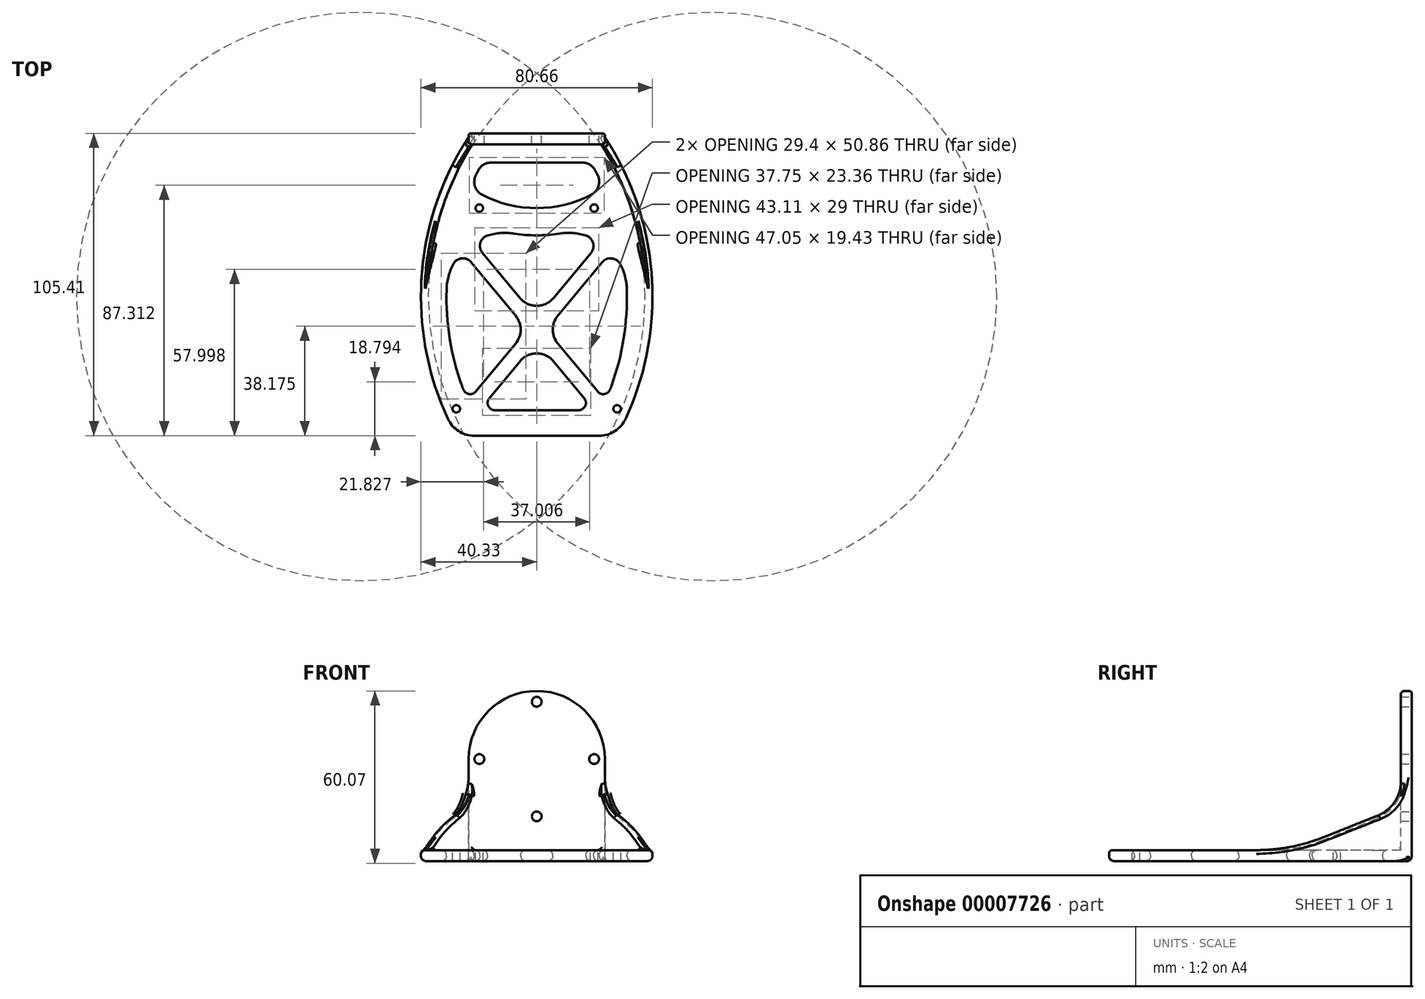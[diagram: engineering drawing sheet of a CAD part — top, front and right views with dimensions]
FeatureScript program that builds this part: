
annotation { "Feature Type Name" : "Feature", "Feature Type Description" : "" }
export const myFeature = defineFeature(function(context is Context, id is Id, definition is map)
    precondition{}
    {
        {
            var Q0;
            Q0=qCreatedBy(makeId("Front.planeOp"),FACE);
            var sketch = newSketch(context, id + "F0", { "sketchPlane" : qUnion([Q0])});
            skCircle(sketch, "E0", {"center": v(0, 19.99) * mm, "radius": 1.7 * mm});
            skCircle(sketch, "E1.1.0", {"center": v(-19.99, 0) * mm, "radius": 1.7 * mm});
            skCircle(sketch, "E1.2.0", {"center": v(0, -19.99) * mm, "radius": 1.7 * mm});
            skCircle(sketch, "E1.3.0", {"center": v(19.99, 0) * mm, "radius": 1.7 * mm});
            skPoint(sketch, "E1.center", {"position": v(0, 0) * mm});
            skArc(sketch, "E2", {"start": v(23.75, 0) * mm, "mid": v(0, 23.75) * mm, "end": v(-23.75, 0) * mm});
            skLineSegment(sketch, "E3.top", {"start": v(-23.75, -31.75) * mm, "end": v(23.75, -31.75) * mm});
            skLineSegment(sketch, "E3.left", {"start": v(-23.75, 0) * mm, "end": v(-23.75, -31.75) * mm});
            skLineSegment(sketch, "E3.right", {"start": v(23.75, 0) * mm, "end": v(23.75, -31.75) * mm});
            skSolve(sketch);
        }
        {
            var Q0;
            Q0 = qSketchRegion(id + "F0", true);
            extrude(context, id + "F1", {"entities" : qUnion([Q0]), "depth" : 2.54 * mm});
        }
        {
            var Q0;
            Q0=makeQuery(id+"F1.opExtrude","SWEPT_FACE",FACE,{"disambiguationData":[OSD([sQuery(id+"F0.wireOp",EDGE,"E3.top")])]});
            var sketch = newSketch(context, id + "F2", { "sketchPlane" : qUnion([Q0])});
            skCircle(sketch, "E4", {"center": v(-20, 24.77) * mm, "radius": 1.3 * mm});
            skCircle(sketch, "E5", {"center": v(-28, 94.77) * mm, "radius": 1.3 * mm});
            skLineSegment(sketch, "E6", {"start": v(-20, 24.77) * mm, "end": v(-20, 0) * mm, "construction": true});
            skLineSegment(sketch, "E7", {"start": v(-28, 94.77) * mm, "end": v(-28, 0) * mm, "construction": true});
            skCircle(sketch, "E8.0.MirrorC", {"center": v(20, 24.77) * mm, "radius": 1.3 * mm});
            skCircle(sketch, "E8.1.MirrorC", {"center": v(28, 94.77) * mm, "radius": 1.3 * mm});
            skArc(sketch, "E9", {"start": v(-30.96, 98.24) * mm, "mid": v(-40.06, 48.19) * mm, "end": v(-23.75, 0) * mm});
            skArc(sketch, "E10.0.MirrorCS", {"start": v(30.96, 98.24) * mm, "mid": v(40.06, 48.19) * mm, "end": v(23.75, 0) * mm});
            skLineSegment(sketch, "E11", {"start": v(-21.74, 104.14) * mm, "end": v(21.74, 104.14) * mm});
            skPoint(sketch, "E12.visualSharp", {"position": v(-28, 104.14) * mm});
            skArc(sketch, "E12.filletArc", {"start": v(-21.74, 104.14) * mm, "mid": v(-27.22, 102.54) * mm, "end": v(-30.96, 98.24) * mm});
            skPoint(sketch, "E13.visualSharp", {"position": v(28, 104.14) * mm});
            skArc(sketch, "E13.filletArc", {"start": v(30.96, 98.24) * mm, "mid": v(27.22, 102.54) * mm, "end": v(21.74, 104.14) * mm});
            skLineSegment(sketch, "E14", {"start": v(-23.75, 0) * mm, "end": v(23.75, 0) * mm});
            skArc(sketch, "E15.0", {"start": v(-26.04, 86.82) * mm, "mid": v(-30.28, 70.26) * mm, "end": v(-31.41, 53.2) * mm});
            skLineSegment(sketch, "E15.1", {"start": v(-14.08, 95.25) * mm, "end": v(14.08, 95.25) * mm});
            skArc(sketch, "E15.2", {"start": v(26.04, 86.82) * mm, "mid": v(30.28, 70.26) * mm, "end": v(31.41, 53.2) * mm});
            skLineSegment(sketch, "E15.3", {"start": v(-15.83, 8.89) * mm, "end": v(15.83, 8.89) * mm});
            skArc(sketch, "E16", {"start": v(7.93, 33.67) * mm, "mid": v(0, 34.3) * mm, "end": v(-7.93, 33.67) * mm});
            skArc(sketch, "E17", {"start": v(19.03, 20.12) * mm, "mid": v(0, 24.77) * mm, "end": v(-19.03, 20.12) * mm});
            skArc(sketch, "E18.trimOffspring", {"start": v(21.2, 13.29) * mm, "mid": v(20.76, 12.42) * mm, "end": v(20.3, 11.55) * mm});
            skArc(sketch, "E19.trimOffspring", {"start": v(-21.2, 13.29) * mm, "mid": v(-20.76, 12.42) * mm, "end": v(-20.3, 11.55) * mm});
            skPoint(sketch, "E20.visualSharp", {"position": v(-26.8, 26.65) * mm});
            skArc(sketch, "E20.filletArc", {"start": v(-31.41, 53.2) * mm, "mid": v(-30.77, 48.64) * mm, "end": v(-29.1, 44.33) * mm});
            skPoint(sketch, "E21.visualSharp", {"position": v(26.8, 26.65) * mm});
            skArc(sketch, "E21.filletArc", {"start": v(7.93, 33.67) * mm, "mid": v(12.55, 33.47) * mm, "end": v(17.1, 34.32) * mm});
            skPoint(sketch, "E22.visualSharp", {"position": v(18.8, 8.89) * mm});
            skArc(sketch, "E22.filletArc", {"start": v(15.83, 8.89) * mm, "mid": v(18.43, 9.6) * mm, "end": v(20.3, 11.55) * mm});
            skPoint(sketch, "E23.visualSharp", {"position": v(-18.8, 8.89) * mm});
            skArc(sketch, "E23.filletArc", {"start": v(-20.3, 11.55) * mm, "mid": v(-18.43, 9.6) * mm, "end": v(-15.83, 8.89) * mm});
            skPoint(sketch, "E24.visualSharp", {"position": v(-23.27, 17.58) * mm});
            skArc(sketch, "E24.filletArc", {"start": v(-19.03, 20.12) * mm, "mid": v(-21.53, 17.15) * mm, "end": v(-21.2, 13.29) * mm});
            skPoint(sketch, "E25.visualSharp", {"position": v(23.27, 17.58) * mm});
            skArc(sketch, "E25.filletArc", {"start": v(21.2, 13.29) * mm, "mid": v(21.53, 17.15) * mm, "end": v(19.03, 20.12) * mm});
            skPoint(sketch, "E26.visualSharp", {"position": v(-22.55, 95.25) * mm});
            skArc(sketch, "E26.filletArc", {"start": v(-14.08, 95.25) * mm, "mid": v(-14.4, 95.25) * mm, "end": v(-14.73, 95.23) * mm});
            skPoint(sketch, "E27.visualSharp", {"position": v(22.55, 95.25) * mm});
            skArc(sketch, "E27.filletArc", {"start": v(26.04, 86.82) * mm, "mid": v(25.76, 87.54) * mm, "end": v(25.43, 88.24) * mm});
            skLineSegment(sketch, "E28", {"start": v(-21.4, 92.93) * mm, "end": v(24.1, 38.12) * mm, "construction": true});
            skLineSegment(sketch, "E29", {"start": v(-24.1, 38.12) * mm, "end": v(21.4, 92.93) * mm, "construction": true});
            skLineSegment(sketch, "E30.0", {"start": v(-21.2, 88.73) * mm, "end": v(-7.34, 72.02) * mm});
            skLineSegment(sketch, "E31.0", {"start": v(-16.55, 91.07) * mm, "end": v(-5.86, 78.2) * mm});
            skLineSegment(sketch, "E32.0", {"start": v(-18.9, 40.4) * mm, "end": v(-5.86, 56.1) * mm});
            skLineSegment(sketch, "E33.0", {"start": v(-22.8, 43.66) * mm, "end": v(-7.34, 62.29) * mm});
            skArc(sketch, "E34.trimOffspring", {"start": v(14.73, 95.23) * mm, "mid": v(14.4, 95.25) * mm, "end": v(14.08, 95.25) * mm});
            skArc(sketch, "E35.trimOffspring", {"start": v(-25.43, 88.24) * mm, "mid": v(-25.76, 87.54) * mm, "end": v(-26.04, 86.82) * mm});
            skLineSegment(sketch, "E36.trimOffspring", {"start": v(5.86, 78.2) * mm, "end": v(16.55, 91.07) * mm});
            skLineSegment(sketch, "E37.trimOffspring", {"start": v(7.34, 62.29) * mm, "end": v(22.8, 43.66) * mm});
            skLineSegment(sketch, "E38.trimOffspring", {"start": v(7.34, 72.02) * mm, "end": v(21.2, 88.73) * mm});
            skLineSegment(sketch, "E39.trimOffspring", {"start": v(5.86, 56.1) * mm, "end": v(18.9, 40.4) * mm});
            skArc(sketch, "E40.trimOffspring", {"start": v(-17.1, 34.32) * mm, "mid": v(-12.55, 33.47) * mm, "end": v(-7.93, 33.67) * mm});
            skArc(sketch, "E41.trimOffspring", {"start": v(29.1, 44.33) * mm, "mid": v(30.77, 48.64) * mm, "end": v(31.41, 53.2) * mm});
            skPoint(sketch, "E42.visualSharp", {"position": v(-3.3, 67.15) * mm});
            skArc(sketch, "E42.filletArc", {"start": v(-7.34, 62.29) * mm, "mid": v(-5.58, 67.15) * mm, "end": v(-7.34, 72.02) * mm});
            skPoint(sketch, "E43.visualSharp", {"position": v(3.3, 67.15) * mm});
            skArc(sketch, "E43.filletArc", {"start": v(7.34, 72.02) * mm, "mid": v(5.58, 67.15) * mm, "end": v(7.34, 62.29) * mm});
            skPoint(sketch, "E44.visualSharp", {"position": v(0, 71.13) * mm});
            skArc(sketch, "E44.filletArc", {"start": v(-5.86, 78.2) * mm, "mid": v(0, 75.44) * mm, "end": v(5.86, 78.2) * mm});
            skPoint(sketch, "E45.visualSharp", {"position": v(0, 63.18) * mm});
            skArc(sketch, "E45.filletArc", {"start": v(5.86, 56.1) * mm, "mid": v(0, 58.86) * mm, "end": v(-5.86, 56.1) * mm});
            skPoint(sketch, "E46.visualSharp", {"position": v(25.95, 39.87) * mm});
            skArc(sketch, "E46.filletArc", {"start": v(22.8, 43.66) * mm, "mid": v(26.13, 42.3) * mm, "end": v(29.1, 44.33) * mm});
            skPoint(sketch, "E47.visualSharp", {"position": v(22.04, 36.62) * mm});
            skArc(sketch, "E47.filletArc", {"start": v(17.1, 34.32) * mm, "mid": v(19.62, 36.88) * mm, "end": v(18.9, 40.4) * mm});
            skPoint(sketch, "E48.visualSharp", {"position": v(-22.04, 36.62) * mm});
            skArc(sketch, "E48.filletArc", {"start": v(-18.9, 40.4) * mm, "mid": v(-19.62, 36.88) * mm, "end": v(-17.1, 34.32) * mm});
            skPoint(sketch, "E49.visualSharp", {"position": v(-25.95, 39.87) * mm});
            skArc(sketch, "E49.filletArc", {"start": v(-29.1, 44.33) * mm, "mid": v(-26.13, 42.3) * mm, "end": v(-22.8, 43.66) * mm});
            skPoint(sketch, "E50.visualSharp", {"position": v(19.14, 94.2) * mm});
            skArc(sketch, "E50.filletArc", {"start": v(16.55, 91.07) * mm, "mid": v(16.92, 93.72) * mm, "end": v(14.73, 95.23) * mm});
            skPoint(sketch, "E51.visualSharp", {"position": v(23.31, 91.27) * mm});
            skArc(sketch, "E51.filletArc", {"start": v(25.43, 88.24) * mm, "mid": v(23.45, 89.63) * mm, "end": v(21.2, 88.73) * mm});
            skPoint(sketch, "E52.visualSharp", {"position": v(-19.14, 94.2) * mm});
            skArc(sketch, "E52.filletArc", {"start": v(-14.73, 95.23) * mm, "mid": v(-16.92, 93.72) * mm, "end": v(-16.55, 91.07) * mm});
            skPoint(sketch, "E53.visualSharp", {"position": v(-23.31, 91.27) * mm});
            skArc(sketch, "E53.filletArc", {"start": v(-21.2, 88.73) * mm, "mid": v(-23.45, 89.63) * mm, "end": v(-25.43, 88.24) * mm});
            skSolve(sketch);
        }
        {
            var Q0;
            Q0 = qSketchRegion(id + "F2", true);
            extrude(context, id + "F3", {"entities" : qUnion([Q0]), "operationType" : NewBodyOperationType.ADD, "depth" : 3.8 * mm});
        }
        {
            var Q0;
            Q0=makeQuery(id+"F3.opExtrude","CAP_FACE",FACE,{"disambiguationData":[OSD([sQuery(id+"F2.wireOp",EDGE,"E4"),sQuery(id+"F2.wireOp",EDGE,"E5"),sQuery(id+"F2.wireOp",EDGE,"E8.0.MirrorC"),sQuery(id+"F2.wireOp",EDGE,"E8.1.MirrorC"),sQuery(id+"F2.wireOp",EDGE,"E9"),sQuery(id+"F2.wireOp",EDGE,"E10.0.MirrorCS"),sQuery(id+"F2.wireOp",EDGE,"E11"),sQuery(id+"F2.wireOp",EDGE,"E12.filletArc"),sQuery(id+"F2.wireOp",EDGE,"E13.filletArc"),sQuery(id+"F2.wireOp",EDGE,"E14"),sQuery(id+"F2.wireOp",EDGE,"E15.0"),sQuery(id+"F2.wireOp",EDGE,"E15.1"),sQuery(id+"F2.wireOp",EDGE,"E15.2"),sQuery(id+"F2.wireOp",EDGE,"E15.3"),sQuery(id+"F2.wireOp",EDGE,"E16"),sQuery(id+"F2.wireOp",EDGE,"E17"),sQuery(id+"F2.wireOp",EDGE,"E18.trimOffspring"),sQuery(id+"F2.wireOp",EDGE,"E19.trimOffspring"),sQuery(id+"F2.wireOp",EDGE,"E20.filletArc"),sQuery(id+"F2.wireOp",EDGE,"E21.filletArc"),sQuery(id+"F2.wireOp",EDGE,"E22.filletArc"),sQuery(id+"F2.wireOp",EDGE,"E23.filletArc"),sQuery(id+"F2.wireOp",EDGE,"E24.filletArc"),sQuery(id+"F2.wireOp",EDGE,"E25.filletArc"),sQuery(id+"F2.wireOp",EDGE,"E26.filletArc"),sQuery(id+"F2.wireOp",EDGE,"E27.filletArc"),sQuery(id+"F2.wireOp",EDGE,"E30.0"),sQuery(id+"F2.wireOp",EDGE,"E31.0"),sQuery(id+"F2.wireOp",EDGE,"E32.0"),sQuery(id+"F2.wireOp",EDGE,"E33.0"),sQuery(id+"F2.wireOp",EDGE,"E34.trimOffspring"),sQuery(id+"F2.wireOp",EDGE,"E35.trimOffspring"),sQuery(id+"F2.wireOp",EDGE,"E36.trimOffspring"),sQuery(id+"F2.wireOp",EDGE,"E37.trimOffspring"),sQuery(id+"F2.wireOp",EDGE,"E38.trimOffspring"),sQuery(id+"F2.wireOp",EDGE,"E39.trimOffspring"),sQuery(id+"F2.wireOp",EDGE,"E40.trimOffspring"),sQuery(id+"F2.wireOp",EDGE,"E41.trimOffspring"),sQuery(id+"F2.wireOp",EDGE,"E42.filletArc"),sQuery(id+"F2.wireOp",EDGE,"E43.filletArc"),sQuery(id+"F2.wireOp",EDGE,"E44.filletArc"),sQuery(id+"F2.wireOp",EDGE,"E45.filletArc"),sQuery(id+"F2.wireOp",EDGE,"E46.filletArc"),sQuery(id+"F2.wireOp",EDGE,"E47.filletArc"),sQuery(id+"F2.wireOp",EDGE,"E48.filletArc"),sQuery(id+"F2.wireOp",EDGE,"E49.filletArc"),sQuery(id+"F2.wireOp",EDGE,"E50.filletArc"),sQuery(id+"F2.wireOp",EDGE,"E51.filletArc"),sQuery(id+"F2.wireOp",EDGE,"E52.filletArc"),sQuery(id+"F2.wireOp",EDGE,"E53.filletArc")])],"isStart":true});
            var sketch = newSketch(context, id + "F4", { "sketchPlane" : qUnion([Q0])});
            skArc(sketch, "E54.0", {"start": v(-40.33, -55.63) * mm, "mid": v(-36.1, -26.6) * mm, "end": v(-23.75, 0) * mm});
            skArc(sketch, "E55.0", {"start": v(-37.8, -55.63) * mm, "mid": v(-33.66, -27.33) * mm, "end": v(-21.62, -1.4) * mm});
            skLineSegment(sketch, "E56", {"start": v(-40.33, -55.63) * mm, "end": v(-37.8, -55.63) * mm});
            skPoint(sketch, "E57.orphan", {"position": v(-30.96, -98.24) * mm});
            skLineSegment(sketch, "E58", {"start": v(-23.75, 0) * mm, "end": v(-21.62, -1.4) * mm});
            skLineSegment(sketch, "E59.0.MirrorCS", {"start": v(40.33, -55.63) * mm, "end": v(37.8, -55.63) * mm});
            skLineSegment(sketch, "E59.1.MirrorCS", {"start": v(23.75, 0) * mm, "end": v(21.62, -1.4) * mm});
            skArc(sketch, "E59.2.MirrorCS", {"start": v(37.8, -55.63) * mm, "mid": v(33.66, -27.33) * mm, "end": v(21.62, -1.4) * mm});
            skArc(sketch, "E59.3.MirrorCS", {"start": v(40.33, -55.63) * mm, "mid": v(36.1, -26.6) * mm, "end": v(23.75, 0) * mm});
            skSolve(sketch);
        }
        {
            var Q0;
            Q0 = qSketchRegion(id + "F4", true);
            extrude(context, id + "F5", {"entities" : qUnion([Q0]), "operationType" : NewBodyOperationType.ADD, "depth" : 25.4 * mm});
        }
        {
            var Q0;
            Q0=qCreatedBy(makeId("Right.planeOp"),FACE);
            cPlane(context, id + "F6", {"entities" : qUnion([Q0]), "cplaneType" : CPlaneType.OFFSET, "offset" : 152.4 * mm, "width" : 152.4 * mm, "height" : 152.4 * mm});
        }
        {
            var Q0;
            Q0=qCreatedBy(id+"F6.planeOp",FACE);
            var sketch = newSketch(context, id + "F7", { "sketchPlane" : qUnion([Q0])});
            skPoint(sketch, "E60.orphan", {"position": v(0, -6.35) * mm});
            skPoint(sketch, "E61.0.end.orphan", {"position": v(-55.63, -6.35) * mm});
            skLineSegment(sketch, "E62", {"start": v(-55.63, -31.75) * mm, "end": v(-52.87, -31.75) * mm});
            skPoint(sketch, "E61.3.start.orphan", {"position": v(-2.54, 0) * mm});
            skLineSegment(sketch, "E63", {"start": v(-2.54, -6.35) * mm, "end": v(-55.63, -6.35) * mm});
            skPoint(sketch, "E61.2.end.orphan", {"position": v(-98.24, -31.75) * mm});
            skLineSegment(sketch, "E64", {"start": v(-55.63, -31.75) * mm, "end": v(-55.63, -6.35) * mm});
            skLineSegment(sketch, "E65", {"start": v(-29.29, -27.2) * mm, "end": v(-10.52, -19.7) * mm});
            skLineSegment(sketch, "E66", {"start": v(-2.54, -6.35) * mm, "end": v(-2.54, -7.91) * mm});
            skPoint(sketch, "E67.start.orphan", {"position": v(-2.54, -31.75) * mm});
            skPoint(sketch, "E68.orphan", {"position": v(-25.65, -31.75) * mm});
            skPoint(sketch, "E69.visualSharp", {"position": v(-2.54, -16.5) * mm});
            skArc(sketch, "E69.filletArc", {"start": v(-10.52, -19.7) * mm, "mid": v(-4.72, -15.03) * mm, "end": v(-2.54, -7.91) * mm});
            skPoint(sketch, "E70.visualSharp", {"position": v(-40.64, -31.75) * mm});
            skArc(sketch, "E70.filletArc", {"start": v(-52.87, -31.75) * mm, "mid": v(-40.86, -30.6) * mm, "end": v(-29.29, -27.2) * mm});
            skSolve(sketch);
        }
        {
            var Q0;
            Q0 = qSketchRegion(id + "F7", true);
            extrude(context, id + "F8", {"entities" : qUnion([Q0]), "operationType" : NewBodyOperationType.REMOVE, "endBound" : BoundingType.THROUGH_ALL, "oppositeDirection" : true, "depth" : 25.4 * mm});
        }
        {
            var Q0;
            Q0=makeQuery(id+"F5.opExtrude","SWEPT_FACE",FACE,{"disambiguationData":[OSD([sQuery(id+"F4.wireOp",EDGE,"E55.0")])]});
            var Q1;
            Q1=makeQuery(id+"F5.opExtrude","SWEPT_FACE",FACE,{"disambiguationData":[OSD([sQuery(id+"F4.wireOp",EDGE,"E59.2.MirrorCS")])]});
            fillet(context, id + "F9", {"entities" : qUnion([Q0, Q1]), "radius" : 1.02 * mm, "tangentPropagation" : true, "allowEdgeOverflow" : false});
        }
        {
            var Q0;
            Q0=makeQuery(id+"F3.boolean.opBoolean","MERGE",FACE,{"derivedFrom":[makeQuery(id+"F1.opExtrude","CAP_FACE",FACE,{"disambiguationData":[OSD([sQuery(id+"F0.wireOp",EDGE,"E0"),sQuery(id+"F0.wireOp",EDGE,"E1.1.0"),sQuery(id+"F0.wireOp",EDGE,"E1.2.0"),sQuery(id+"F0.wireOp",EDGE,"E1.3.0"),sQuery(id+"F0.wireOp",EDGE,"E2"),sQuery(id+"F0.wireOp",EDGE,"E3.top"),sQuery(id+"F0.wireOp",EDGE,"E3.left"),sQuery(id+"F0.wireOp",EDGE,"E3.right")])],"isStart":true}),makeQuery(id+"F3.opExtrude","SWEPT_FACE",FACE,{"disambiguationData":[OSD([sQuery(id+"F2.wireOp",EDGE,"E14")])]})]});
            var sketch = newSketch(context, id + "F10", { "sketchPlane" : qUnion([Q0])});
            skFitSpline(sketch, "E71.0", {"points": [v(29.77, -19.7) * mm, v(29.5, -19.48) * mm, v(29.22, -19.22) * mm, v(28.95, -18.91) * mm, v(28.67, -18.61) * mm, v(28.4, -18.27) * mm, v(28.15, -17.9) * mm, v(27.9, -17.52) * mm, v(27.64, -17.1) * mm, v(27.4, -16.66) * mm, v(27.16, -16.2) * mm, v(26.94, -15.73) * mm, v(26.74, -15.23) * mm, v(26.52, -14.7) * mm, v(26.33, -14.16) * mm, v(26.17, -13.6) * mm, v(26, -13.01) * mm, v(25.85, -12.42) * mm, v(25.73, -11.8) * mm, v(25.6, -11.18) * mm, v(25.52, -10.55) * mm, v(25.45, -9.9) * mm, v(25.39, -9.24) * mm, v(25.36, -8.58) * mm, v(25.36, -7.91) * mm]});
            skLineSegment(sketch, "E71.1", {"start": v(25.36, -6.35) * mm, "end": v(25.36, -7.91) * mm});
            skFitSpline(sketch, "E71.6.3", {"points": [v(29.77, -19.7) * mm, v(29.5, -19.48) * mm, v(29.22, -19.22) * mm, v(28.95, -18.91) * mm, v(28.67, -18.61) * mm, v(28.4, -18.27) * mm, v(28.15, -17.9) * mm, v(27.9, -17.52) * mm, v(27.64, -17.1) * mm, v(27.4, -16.66) * mm, v(27.16, -16.2) * mm, v(26.94, -15.73) * mm, v(26.74, -15.23) * mm, v(26.52, -14.7) * mm, v(26.33, -14.16) * mm, v(26.17, -13.6) * mm, v(26, -13.01) * mm, v(25.85, -12.42) * mm, v(25.73, -11.8) * mm, v(25.6, -11.18) * mm, v(25.52, -10.55) * mm, v(25.45, -9.9) * mm, v(25.39, -9.24) * mm, v(25.36, -8.58) * mm, v(25.36, -7.91) * mm]});
            skLineSegment(sketch, "E71.6.4", {"start": v(25.36, -6.35) * mm, "end": v(25.36, -7.91) * mm});
            skArc(sketch, "E72", {"start": v(23.75, -6.35) * mm, "mid": v(25.32, -13.67) * mm, "end": v(29.77, -19.7) * mm});
            skLineSegment(sketch, "E73", {"start": v(23.75, -6.35) * mm, "end": v(25.36, -6.35) * mm});
            skLineSegment(sketch, "E74.0.MirrorCS", {"start": v(-23.75, -6.35) * mm, "end": v(-25.36, -6.35) * mm});
            skArc(sketch, "E75.0.MirrorCS", {"start": v(-23.75, -6.35) * mm, "mid": v(-25.32, -13.67) * mm, "end": v(-29.77, -19.7) * mm});
            skFitSpline(sketch, "E76.0.MirrorCS", {"points": [v(-29.77, -19.7) * mm, v(-29.5, -19.48) * mm, v(-29.22, -19.22) * mm, v(-28.95, -18.91) * mm, v(-28.67, -18.61) * mm, v(-28.4, -18.27) * mm, v(-28.15, -17.9) * mm, v(-27.9, -17.52) * mm, v(-27.64, -17.1) * mm, v(-27.4, -16.66) * mm, v(-27.16, -16.2) * mm, v(-26.94, -15.73) * mm, v(-26.74, -15.23) * mm, v(-26.52, -14.7) * mm, v(-26.33, -14.16) * mm, v(-26.17, -13.6) * mm, v(-26, -13.01) * mm, v(-25.85, -12.42) * mm, v(-25.73, -11.8) * mm, v(-25.6, -11.18) * mm, v(-25.52, -10.55) * mm, v(-25.45, -9.9) * mm, v(-25.39, -9.24) * mm, v(-25.36, -8.58) * mm, v(-25.36, -7.91) * mm]});
            skLineSegment(sketch, "E77.0.MirrorCS", {"start": v(-25.36, -6.35) * mm, "end": v(-25.36, -7.91) * mm});
            skSolve(sketch);
        }
        {
            var Q0;
            Q0 = qSketchRegion(id + "F10", true);
            extrude(context, id + "F11", {"entities" : qUnion([Q0]), "operationType" : NewBodyOperationType.REMOVE, "endBound" : BoundingType.THROUGH_ALL, "oppositeDirection" : true, "depth" : 25.4 * mm});
        }
        {
            var Q0;
            Q0=makeQuery(id+"F3.boolean.opBoolean","MERGE",FACE,{"derivedFrom":[makeQuery(id+"F1.opExtrude","CAP_FACE",FACE,{"disambiguationData":[OSD([sQuery(id+"F0.wireOp",EDGE,"E0"),sQuery(id+"F0.wireOp",EDGE,"E1.1.0"),sQuery(id+"F0.wireOp",EDGE,"E1.2.0"),sQuery(id+"F0.wireOp",EDGE,"E1.3.0"),sQuery(id+"F0.wireOp",EDGE,"E2"),sQuery(id+"F0.wireOp",EDGE,"E3.top"),sQuery(id+"F0.wireOp",EDGE,"E3.left"),sQuery(id+"F0.wireOp",EDGE,"E3.right")])],"isStart":true}),makeQuery(id+"F3.opExtrude","SWEPT_FACE",FACE,{"disambiguationData":[OSD([sQuery(id+"F2.wireOp",EDGE,"E14")])]})]});
            var sketch = newSketch(context, id + "F12", { "sketchPlane" : qUnion([Q0])});
            skArc(sketch, "E78.0", {"start": v(-23.75, 0) * mm, "mid": v(0, 23.75) * mm, "end": v(23.75, 0) * mm});
            skLineSegment(sketch, "E78.1", {"start": v(-23.75, -35.56) * mm, "end": v(-23.75, -6.35) * mm});
            skLineSegment(sketch, "E78.2", {"start": v(-23.75, 0) * mm, "end": v(-23.75, -6.35) * mm});
            skLineSegment(sketch, "E78.3", {"start": v(23.75, 0) * mm, "end": v(23.75, -6.35) * mm});
            skLineSegment(sketch, "E78.4", {"start": v(23.75, -35.56) * mm, "end": v(23.75, -6.35) * mm});
            skLineSegment(sketch, "E78.5", {"start": v(23.75, -35.56) * mm, "end": v(-23.75, -35.56) * mm});
            skCircle(sketch, "E78.6", {"center": v(0, -19.99) * mm, "radius": 1.7 * mm});
            skCircle(sketch, "E78.7", {"center": v(19.99, 0) * mm, "radius": 1.7 * mm});
            skCircle(sketch, "E78.8", {"center": v(0, 19.99) * mm, "radius": 1.7 * mm});
            skCircle(sketch, "E78.9", {"center": v(-19.99, 0) * mm, "radius": 1.7 * mm});
            skSolve(sketch);
        }
        {
            var Q0;
            Q0 = qSketchRegion(id + "F12", true);
            extrude(context, id + "F13", {"entities" : qUnion([Q0]), "operationType" : NewBodyOperationType.ADD, "depth" : 1.27 * mm});
        }
        {
            var Q0;
            Q0=makeQuery(id+"F3.opExtrude","CAP_EDGE",EDGE,{"disambiguationData":[OSD([sQuery(id+"F2.wireOp",EDGE,"E15.3")])],"isStart":true});
            var Q1;
            Q1=makeQuery(id+"F3.opExtrude","CAP_EDGE",EDGE,{"disambiguationData":[OSD([sQuery(id+"F2.wireOp",EDGE,"E15.3")])],"isStart":false});
            var Q2;
            Q2=makeQuery(id+"F3.opExtrude","CAP_EDGE",EDGE,{"disambiguationData":[OSD([sQuery(id+"F2.wireOp",EDGE,"E16")])],"isStart":true});
            var Q3;
            Q3=makeQuery(id+"F3.opExtrude","CAP_EDGE",EDGE,{"disambiguationData":[OSD([sQuery(id+"F2.wireOp",EDGE,"E16")])],"isStart":false});
            var Q4;
            Q4=makeQuery(id+"F3.opExtrude","CAP_EDGE",EDGE,{"disambiguationData":[OSD([sQuery(id+"F2.wireOp",EDGE,"E37.trimOffspring")])],"isStart":true});
            var Q5;
            Q5=makeQuery(id+"F3.opExtrude","CAP_EDGE",EDGE,{"disambiguationData":[OSD([sQuery(id+"F2.wireOp",EDGE,"E37.trimOffspring")])],"isStart":false});
            var Q6;
            Q6=makeQuery(id+"F3.opExtrude","CAP_EDGE",EDGE,{"disambiguationData":[OSD([sQuery(id+"F2.wireOp",EDGE,"E20.filletArc")])],"isStart":true});
            var Q7;
            Q7=makeQuery(id+"F3.opExtrude","CAP_EDGE",EDGE,{"disambiguationData":[OSD([sQuery(id+"F2.wireOp",EDGE,"E20.filletArc")])],"isStart":false});
            var Q8;
            Q8=makeQuery(id+"F3.opExtrude","CAP_EDGE",EDGE,{"disambiguationData":[OSD([sQuery(id+"F2.wireOp",EDGE,"E31.0")])],"isStart":true});
            var Q9;
            Q9=makeQuery(id+"F3.opExtrude","CAP_EDGE",EDGE,{"disambiguationData":[OSD([sQuery(id+"F2.wireOp",EDGE,"E31.0")])],"isStart":false});
            var Q10;
            Q10=makeQuery(id+"F3.opExtrude","CAP_EDGE",EDGE,{"disambiguationData":[OSD([sQuery(id+"F2.wireOp",EDGE,"E10.0.MirrorCS")])],"isStart":false});
            fillet(context, id + "F14", {"entities" : qUnion([Q0, Q1, Q2, Q3, Q4, Q5, Q6, Q7, Q8, Q9, Q10]), "radius" : 1.78 * mm, "tangentPropagation" : true, "allowEdgeOverflow" : false});
        }
        {
            var Q0;
            Q0=makeQuery(id+"F1.opExtrude","CAP_EDGE",EDGE,{"disambiguationData":[OSD([sQuery(id+"F0.wireOp",EDGE,"E2")])],"isStart":false});
            var Q1;
            Q1=makeQuery(id+"F3.opExtrude","CAP_EDGE",EDGE,{"disambiguationData":[OSD([sQuery(id+"F2.wireOp",EDGE,"E13.filletArc")])],"isStart":true});
            fillet(context, id + "F15", {"entities" : qUnion([Q0, Q1]), "radius" : 1.27 * mm, "tangentPropagation" : true, "allowEdgeOverflow" : false});
        }
        {
            var Q0;
            Q0=makeQuery(id+"F1.opExtrude","CAP_EDGE",EDGE,{"disambiguationData":[OSD([sQuery(id+"F0.wireOp",EDGE,"E3.top")])],"isStart":false});
            var Q1;
            Q1=makeQuery(id+"F13.opExtrude","CAP_EDGE",EDGE,{"disambiguationData":[OSD([sQuery(id+"F12.wireOp",EDGE,"E78.1"),sQuery(id+"F12.wireOp",EDGE,"E78.2")])],"isStart":false});
            var Q2;
            {var subQ0=sQuery(id+"F0.wireOp",EDGE,"E3.right");var subQ1=sQuery(id+"F0.wireOp",EDGE,"E3.top");Q2=makeQuery(id+"F13.boolean.opBoolean","MERGE",EDGE,{"derivedFrom":[makeQuery(id+"F5.boolean.opBoolean","MERGE",EDGE,{"derivedFrom":[makeQuery(id+"F1.opExtrude","CAP_EDGE",EDGE,{"disambiguationData":[OSD([subQ0])],"isStart":true}),makeQuery(id+"F3.opExtrude","SWEPT_EDGE",EDGE,{"disambiguationData":[OSD([subQ1,subQ0,sQuery(id+"F2.wireOp",EDGE,"E10.0.MirrorCS"),sQuery(id+"F2.wireOp",EDGE,"E14")])]}),makeQuery(id+"F5.opExtrude","SWEPT_EDGE",EDGE,{"disambiguationData":[OSD([subQ1,subQ0,sQuery(id+"F4.wireOp",EDGE,"E59.1.MirrorCS"),sQuery(id+"F4.wireOp",EDGE,"E59.3.MirrorCS")])]})]}),makeQuery(id+"F13.opExtrude","CAP_EDGE",EDGE,{"disambiguationData":[OSD([sQuery(id+"F12.wireOp",EDGE,"E78.1"),sQuery(id+"F12.wireOp",EDGE,"E78.2")])],"isStart":true})]});}
            var Q3;
            {var subQ0=sQuery(id+"F0.wireOp",EDGE,"E3.left");var subQ1=sQuery(id+"F0.wireOp",EDGE,"E3.top");Q3=makeQuery(id+"F13.boolean.opBoolean","MERGE",EDGE,{"derivedFrom":[makeQuery(id+"F5.boolean.opBoolean","MERGE",EDGE,{"derivedFrom":[makeQuery(id+"F1.opExtrude","CAP_EDGE",EDGE,{"disambiguationData":[OSD([subQ0])],"isStart":true}),makeQuery(id+"F3.opExtrude","SWEPT_EDGE",EDGE,{"disambiguationData":[OSD([subQ1,subQ0,sQuery(id+"F2.wireOp",EDGE,"E9"),sQuery(id+"F2.wireOp",EDGE,"E14")])]}),makeQuery(id+"F5.opExtrude","SWEPT_EDGE",EDGE,{"disambiguationData":[OSD([subQ1,subQ0,sQuery(id+"F4.wireOp",EDGE,"E54.0"),sQuery(id+"F4.wireOp",EDGE,"E58")])]})]}),makeQuery(id+"F13.opExtrude","CAP_EDGE",EDGE,{"disambiguationData":[OSD([sQuery(id+"F12.wireOp",EDGE,"E78.3"),sQuery(id+"F12.wireOp",EDGE,"E78.4")])],"isStart":true})]});}
            fillet(context, id + "F16", {"entities" : qUnion([Q0, Q1, Q2, Q3]), "radius" : 0.76 * mm, "tangentPropagation" : true, "allowEdgeOverflow" : false});
        }
        {
            var Q0;
            Q0=makeQuery(id+"F13.opExtrude","CAP_EDGE",EDGE,{"disambiguationData":[OSD([sQuery(id+"F12.wireOp",EDGE,"E78.5")])],"isStart":false});
            fillet(context, id + "F17", {"entities" : qUnion([Q0]), "radius" : 1.52 * mm, "tangentPropagation" : true, "allowEdgeOverflow" : false});
        }
    });
